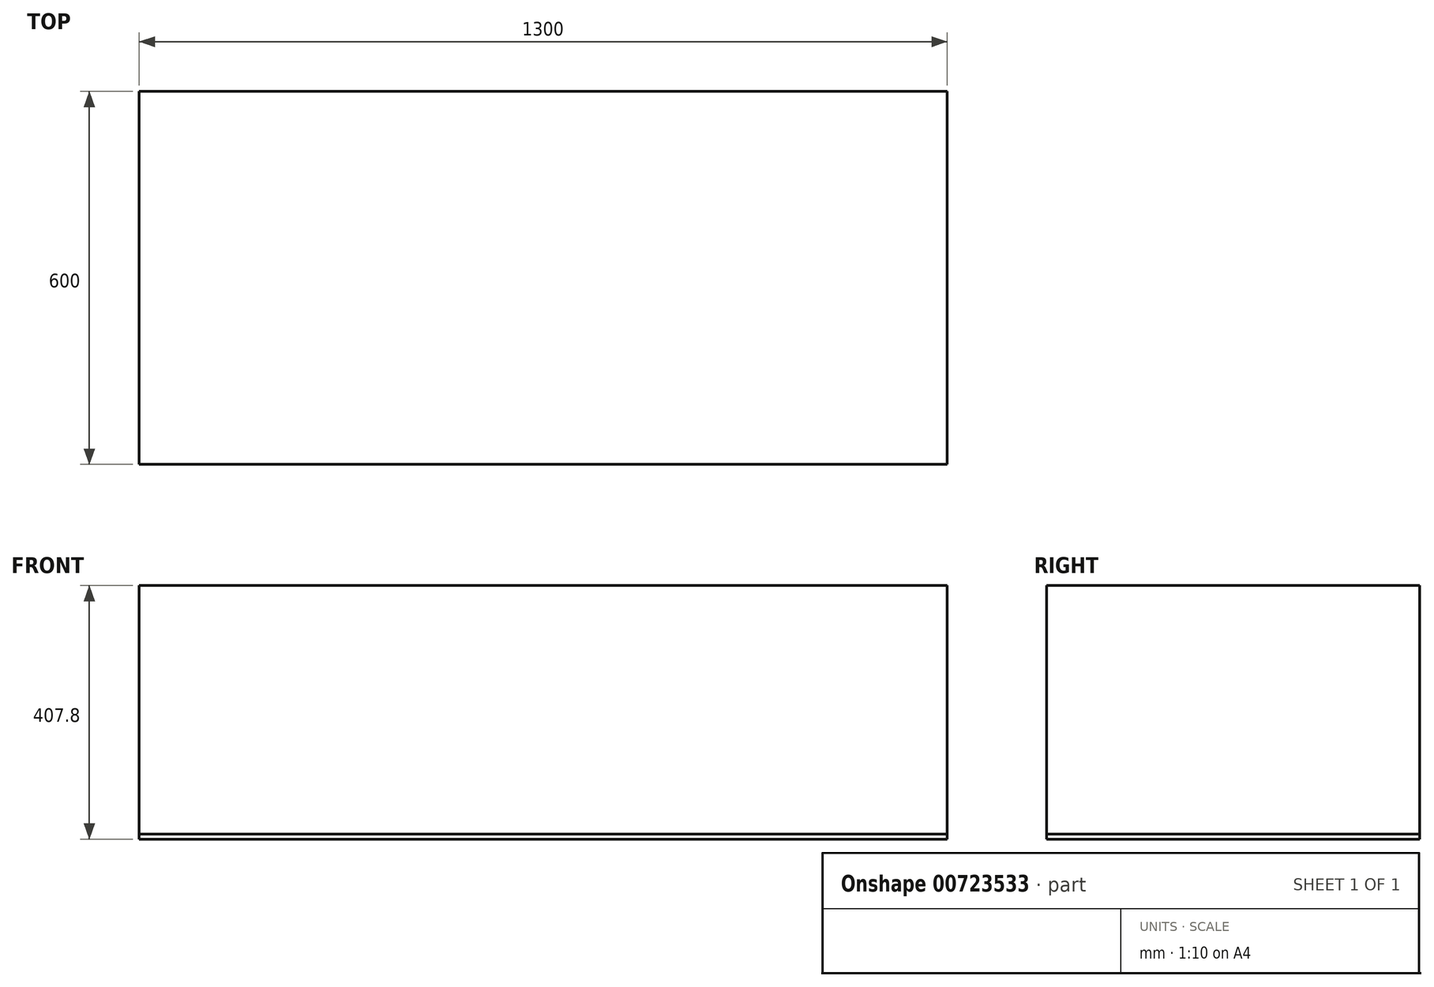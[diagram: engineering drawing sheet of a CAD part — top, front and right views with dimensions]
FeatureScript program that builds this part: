
annotation { "Feature Type Name" : "Feature", "Feature Type Description" : "" }
export const myFeature = defineFeature(function(context is Context, id is Id, definition is map)
    precondition{}
    {
        {
            var Q0;
            Q0=qCreatedBy(makeId("Top.planeOp"),FACE);
            cPlane(context, id + "F0", {"entities" : qUnion([Q0]), "cplaneType" : CPlaneType.OFFSET, "offset" : 6 * mm, "width" : 150 * mm, "height" : 150 * mm});
        }
        {
            var Q0;
            Q0=qCreatedBy(id+"F0.planeOp",FACE);
            var sketch = newSketch(context, id + "F1", { "sketchPlane" : qUnion([Q0])});
            skLineSegment(sketch, "E0.bottom", {"start": v(650, 300) * mm, "end": v(-650, 300) * mm});
            skLineSegment(sketch, "E0.top", {"start": v(650, -300) * mm, "end": v(-650, -300) * mm});
            skLineSegment(sketch, "E0.left", {"start": v(650, 300) * mm, "end": v(650, -300) * mm});
            skLineSegment(sketch, "E0.right", {"start": v(-650, 300) * mm, "end": v(-650, -300) * mm});
            skPoint(sketch, "E0.middle", {"position": v(0, 0) * mm});
            skSolve(sketch);
        }
        {
            var Q0;
            Q0=makeQuery(id+"F1.imprint","IMPRINT",FACE,{"disambiguationData":[TD([[makeQuery(id+"F1.imprint","IMPRINT",EDGE,{"derivedFrom":sQuery(id+"F1.wireOp",EDGE,"E0.bottom")}),1.0]])]});
            extrude(context, id + "F2", {"entities" : qUnion([Q0]), "depth" : 400 * mm, "offsetDistance" : 25 * mm});
        }
        {
            var Q0;
            Q0=makeQuery(id+"F2.opExtrude","CAP_FACE",FACE,{"disambiguationData":[OSD([sQuery(id+"F1.wireOp",EDGE,"E0.bottom"),sQuery(id+"F1.wireOp",EDGE,"E0.top"),sQuery(id+"F1.wireOp",EDGE,"E0.left"),sQuery(id+"F1.wireOp",EDGE,"E0.right")])],"isStart":true});
            var sketch = newSketch(context, id + "F3", { "sketchPlane" : qUnion([Q0])});
            skLineSegment(sketch, "E1.0.0", {"start": v(650, 300) * mm, "end": v(-650, 300) * mm});
            skLineSegment(sketch, "E1.0.1", {"start": v(-650, 300) * mm, "end": v(-650, -300) * mm});
            skLineSegment(sketch, "E1.0.2", {"start": v(-650, -300) * mm, "end": v(650, -300) * mm});
            skLineSegment(sketch, "E1.0.3", {"start": v(650, -300) * mm, "end": v(650, 300) * mm});
            skSolve(sketch);
        }
        {
            var Q0;
            Q0=makeQuery(id+"F3.imprint","IMPRINT",FACE,{"disambiguationData":[TD([[makeQuery(id+"F3.imprint","IMPRINT",EDGE,{"derivedFrom":sQuery(id+"F3.wireOp",EDGE,"E1.0.0")}),1.0]])]});
            var Q1;
            Q1=makeQuery(id+"F3.imprint","IMPRINT",FACE,{"disambiguationData":[TD([[makeQuery(id+"F3.imprint","IMPRINT",EDGE,{"derivedFrom":sQuery(id+"F3.wireOp",EDGE,"E1.0.0")}),-1.0]])]});
            extrude(context, id + "F4", {"entities" : qUnion([Q0, Q1]), "depth" : 7.8 * mm, "offsetDistance" : 25 * mm});
        }
    });
